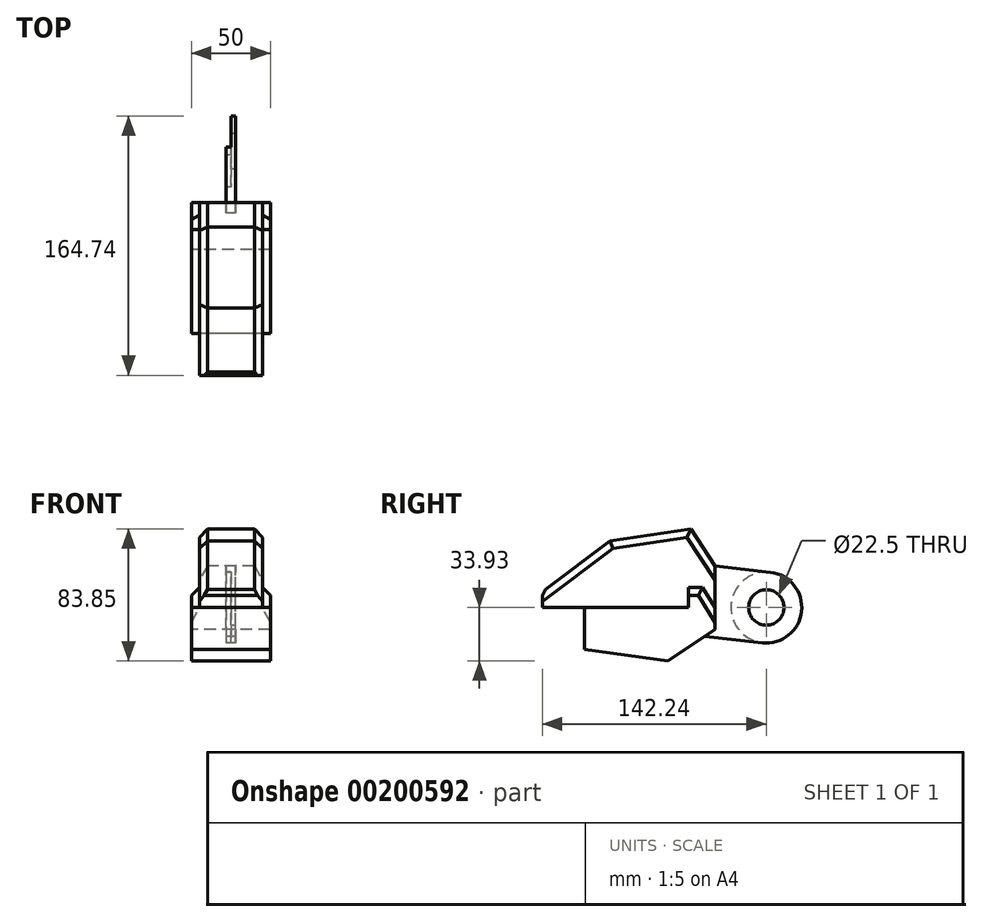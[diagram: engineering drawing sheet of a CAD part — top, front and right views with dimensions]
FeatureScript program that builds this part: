
annotation { "Feature Type Name" : "Feature", "Feature Type Description" : "" }
export const myFeature = defineFeature(function(context is Context, id is Id, definition is map)
    precondition{}
    {
        {
            var Q0;
            Q0=qCreatedBy(makeId("Right.planeOp"),FACE);
            var sketch = newSketch(context, id + "F0", { "sketchPlane" : qUnion([Q0])});
            skCircle(sketch, "E0", {"center": v(32.5, 0) * mm, "radius": 22.5 * mm});
            skLineSegment(sketch, "E1", {"start": v(0, 26.47) * mm, "end": v(35.13, 22.35) * mm});
            skCircle(sketch, "E2", {"center": v(32.5, 0) * mm, "radius": 11.25 * mm});
            skLineSegment(sketch, "E3", {"start": v(0, 26.47) * mm, "end": v(-15.47, 49.92) * mm});
            skLineSegment(sketch, "E4", {"start": v(0, 0) * mm, "end": v(0, 26.47) * mm});
            skPoint(sketch, "E5.orphan", {"position": v(-100, 0) * mm});
            skLineSegment(sketch, "E6", {"start": v(0, 0) * mm, "end": v(0, -14.03) * mm});
            skLineSegment(sketch, "E7", {"start": v(0, -14.03) * mm, "end": v(-29.85, -33.93) * mm});
            skLineSegment(sketch, "E8", {"start": v(-29.85, -33.93) * mm, "end": v(-83.01, -26.54) * mm});
            skLineSegment(sketch, "E9", {"start": v(-83.01, -26.54) * mm, "end": v(-83.01, 0) * mm});
            skLineSegment(sketch, "E10", {"start": v(-83.01, 0) * mm, "end": v(-17.05, 0) * mm});
            skLineSegment(sketch, "E11", {"start": v(-17.05, 0) * mm, "end": v(-17.05, 12.7) * mm});
            skLineSegment(sketch, "E12", {"start": v(-17.05, 12.7) * mm, "end": v(-7.96, 12.7) * mm});
            skLineSegment(sketch, "E13", {"start": v(-7.96, 12.7) * mm, "end": v(0, 0) * mm});
            skLineSegment(sketch, "E14", {"start": v(-15.47, 49.92) * mm, "end": v(-66.8, 42.15) * mm});
            skLineSegment(sketch, "E15", {"start": v(-66.8, 42.15) * mm, "end": v(-109.74, 10.02) * mm});
            skLineSegment(sketch, "E16", {"start": v(-109.74, 10.02) * mm, "end": v(-109.74, 0) * mm});
            skLineSegment(sketch, "E17", {"start": v(-109.74, 0) * mm, "end": v(-83.01, 0) * mm});
            skLineSegment(sketch, "E18", {"start": v(-6.56, -18.4) * mm, "end": v(30.08, -22.37) * mm});
            skSolve(sketch);
        }
        {
            var Q0;
            Q0=makeQuery(id+"F0.imprint","IMPRINT",FACE,{"disambiguationData":[TD([[makeQuery(id+"F0.imprint","IMPRINT",EDGE,{"derivedFrom":sQuery(id+"F0.wireOp",EDGE,"E3")}),1.0]])]});
            extrude(context, id + "F1", {"entities" : qUnion([Q0]), "depth" : 20 * mm, "hasSecondDirection" : true, "secondDirectionOppositeDirection" : true, "secondDirectionDepth" : 20 * mm});
        }
        {
            var Q0;
            {var subQ3=sQuery(id+"F0.wireOp",EDGE,"E6");Q0=makeQuery(id+"F0.imprint","IMPRINT",FACE,{"disambiguationData":[TD([[makeQuery(id+"F0.imprint","IMPRINT",EDGE,{"derivedFrom":subQ3}),-1.0]])]});}
            extrude(context, id + "F2", {"entities" : qUnion([Q0]), "operationType" : NewBodyOperationType.ADD, "depth" : 25 * mm, "hasSecondDirection" : true, "secondDirectionOppositeDirection" : true, "secondDirectionDepth" : 25 * mm});
        }
        {
            var Q0;
            {var subQ4=sQuery(id+"F0.wireOp",EDGE,"E4");Q0=makeQuery(id+"F0.imprint","IMPRINT",FACE,{"disambiguationData":[TD([[makeQuery(id+"F0.imprint","IMPRINT",EDGE,{"derivedFrom":subQ4}),-1.0]])]});}
            extrude(context, id + "F3", {"entities" : qUnion([Q0]), "depth" : 3 * mm, "hasSecondDirection" : true, "secondDirectionOppositeDirection" : true, "secondDirectionDepth" : 3 * mm});
        }
        {
            var Q0;
            Q0=makeQuery(id+"F0.imprint","IMPRINT",FACE,{"disambiguationData":[TD([[makeQuery(id+"F0.imprint","IMPRINT",EDGE,{"derivedFrom":sQuery(id+"F0.wireOp",EDGE,"E2")}),-1.0]])]});
            extrude(context, id + "F4", {"entities" : qUnion([Q0]), "operationType" : NewBodyOperationType.ADD, "depth" : 3 * mm});
        }
        {
            var Q0;
            Q0=makeQuery(id+"F1.opExtrude","CAP_EDGE",EDGE,{"disambiguationData":[OSD([sQuery(id+"F0.wireOp",EDGE,"E15")])],"isStart":false});
            var Q1;
            Q1=makeQuery(id+"F1.opExtrude","SWEPT_EDGE",EDGE,{"disambiguationData":[OSD([sQuery(id+"F0.wireOp",EDGE,"E15"),sQuery(id+"F0.wireOp",EDGE,"E16")])]});
            var Q2;
            Q2=makeQuery(id+"F1.opExtrude","CAP_EDGE",EDGE,{"disambiguationData":[OSD([sQuery(id+"F0.wireOp",EDGE,"E15")])],"isStart":true});
            var Q3;
            Q3=makeQuery(id+"F1.opExtrude","CAP_EDGE",EDGE,{"disambiguationData":[OSD([sQuery(id+"F0.wireOp",EDGE,"E14")])],"isStart":false});
            var Q4;
            Q4=makeQuery(id+"F1.opExtrude","CAP_EDGE",EDGE,{"disambiguationData":[OSD([sQuery(id+"F0.wireOp",EDGE,"E14")])],"isStart":true});
            var Q5;
            Q5=makeQuery(id+"F1.opExtrude","CAP_EDGE",EDGE,{"disambiguationData":[OSD([sQuery(id+"F0.wireOp",EDGE,"E3")])],"isStart":false});
            var Q6;
            Q6=makeQuery(id+"F1.opExtrude","CAP_EDGE",EDGE,{"disambiguationData":[OSD([sQuery(id+"F0.wireOp",EDGE,"E3")])],"isStart":true});
            var Q7;
            Q7=makeQuery(id+"F2.opExtrude","CAP_EDGE",EDGE,{"disambiguationData":[OSD([sQuery(id+"F0.wireOp",EDGE,"E13")])],"isStart":false});
            var Q8;
            Q8=makeQuery(id+"F2.opExtrude","CAP_EDGE",EDGE,{"disambiguationData":[OSD([sQuery(id+"F0.wireOp",EDGE,"E12")])],"isStart":false});
            var Q9;
            Q9=makeQuery(id+"F2.opExtrude","CAP_EDGE",EDGE,{"disambiguationData":[OSD([sQuery(id+"F0.wireOp",EDGE,"E12")])],"isStart":true});
            var Q10;
            Q10=makeQuery(id+"F2.opExtrude","CAP_EDGE",EDGE,{"disambiguationData":[OSD([sQuery(id+"F0.wireOp",EDGE,"E13")])],"isStart":true});
            chamfer(context, id + "F5", {"entities" : qUnion([Q0, Q1, Q2, Q3, Q4, Q5, Q6, Q7, Q8, Q9, Q10]), "width" : 5 * mm, "tangentPropagation" : true});
        }
    });
